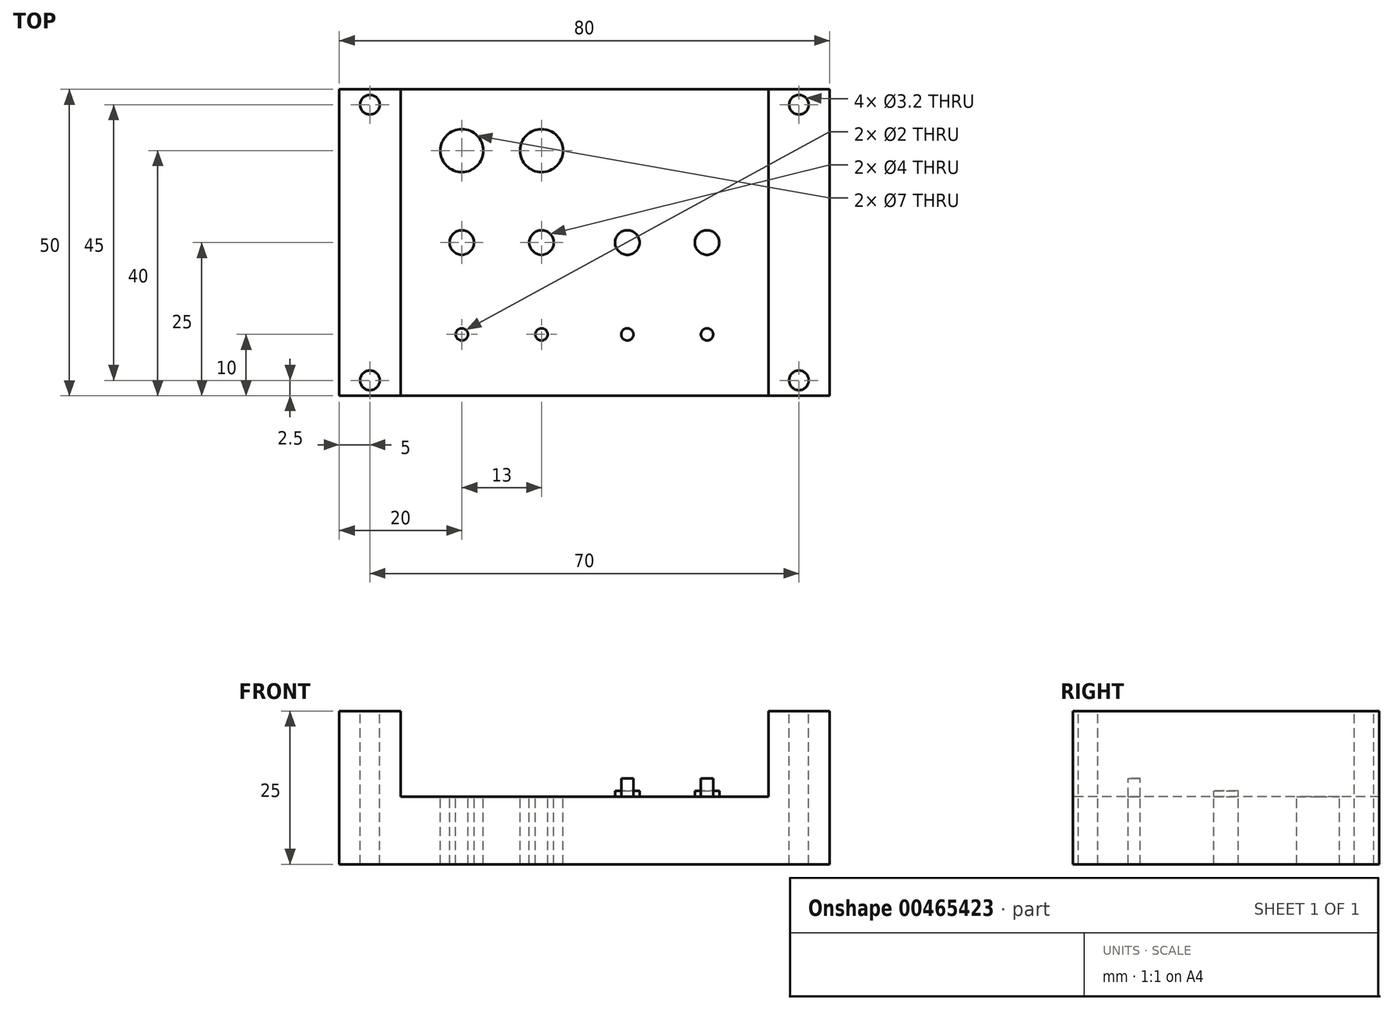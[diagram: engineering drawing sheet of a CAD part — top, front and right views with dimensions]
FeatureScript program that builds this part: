
annotation { "Feature Type Name" : "Feature", "Feature Type Description" : "" }
export const myFeature = defineFeature(function(context is Context, id is Id, definition is map)
    precondition{}
    {
        {
            var Q0;
            Q0=qCreatedBy(makeId("Top.planeOp"),FACE);
            var sketch = newSketch(context, id + "F0", { "sketchPlane" : qUnion([Q0])});
            skLineSegment(sketch, "E0.bottom", {"start": v(40, -25) * mm, "end": v(-40, -25) * mm});
            skLineSegment(sketch, "E0.top", {"start": v(40, 25) * mm, "end": v(-40, 25) * mm});
            skLineSegment(sketch, "E0.left", {"start": v(40, -25) * mm, "end": v(40, 25) * mm});
            skLineSegment(sketch, "E0.right", {"start": v(-40, -25) * mm, "end": v(-40, 25) * mm});
            skPoint(sketch, "E0.middle", {"position": v(0, 0) * mm});
            skLineSegment(sketch, "E1.bottom", {"start": v(30, 25) * mm, "end": v(40, 25) * mm});
            skLineSegment(sketch, "E1.top", {"start": v(30, -25) * mm, "end": v(40, -25) * mm});
            skLineSegment(sketch, "E1.left", {"start": v(30, 25) * mm, "end": v(30, -25) * mm});
            skLineSegment(sketch, "E1.right", {"start": v(40, 25) * mm, "end": v(40, -25) * mm});
            skCircle(sketch, "E2", {"center": v(7, -15) * mm, "radius": 1 * mm});
            skCircle(sketch, "E3", {"center": v(20, -15) * mm, "radius": 1 * mm});
            skCircle(sketch, "E4", {"center": v(7, 0) * mm, "radius": 2 * mm});
            skCircle(sketch, "E5", {"center": v(20, 0) * mm, "radius": 2 * mm});
            skCircle(sketch, "E6", {"center": v(7, 15) * mm, "radius": 3.5 * mm});
            skCircle(sketch, "E7", {"center": v(20, 15) * mm, "radius": 3.5 * mm});
            skLineSegment(sketch, "E8", {"start": v(7, -25) * mm, "end": v(7, 25) * mm, "construction": true});
            skLineSegment(sketch, "E9", {"start": v(20, -25) * mm, "end": v(20, 25) * mm, "construction": true});
            skCircle(sketch, "E10", {"center": v(35, -22.5) * mm, "radius": 1.6 * mm});
            skLineSegment(sketch, "E11", {"start": v(0, -15) * mm, "end": v(30, -15) * mm, "construction": true});
            skLineSegment(sketch, "E12.MirrorCS", {"start": v(0, 15) * mm, "end": v(30, 15) * mm, "construction": true});
            skLineSegment(sketch, "E13", {"start": v(30, -22.5) * mm, "end": v(40, -22.5) * mm, "construction": true});
            skCircle(sketch, "E14.MirrorC", {"center": v(35, 22.5) * mm, "radius": 1.6 * mm});
            skCircle(sketch, "E15.MirrorC", {"center": v(-7, 15) * mm, "radius": 3.5 * mm});
            skCircle(sketch, "E16.MirrorC", {"center": v(-20, 15) * mm, "radius": 3.5 * mm});
            skCircle(sketch, "E17.MirrorC", {"center": v(-7, 0) * mm, "radius": 2 * mm});
            skCircle(sketch, "E18.MirrorC", {"center": v(-20, 0) * mm, "radius": 2 * mm});
            skCircle(sketch, "E19.MirrorC", {"center": v(-7, -15) * mm, "radius": 1 * mm});
            skCircle(sketch, "E20.MirrorC", {"center": v(-20, -15) * mm, "radius": 1 * mm});
            skLineSegment(sketch, "E21.MirrorCS", {"start": v(-30, 25) * mm, "end": v(-30, -25) * mm});
            skCircle(sketch, "E22.MirrorC", {"center": v(-35, 22.5) * mm, "radius": 1.6 * mm});
            skCircle(sketch, "E23.MirrorC", {"center": v(-35, -22.5) * mm, "radius": 1.6 * mm});
            skSolve(sketch);
        }
        {
            var Q0;
            {var subQ0=sQuery(id+"F0.wireOp",EDGE,"E1.left");var subQ1=makeQuery(id+"F0.imprint","IMPRINT",EDGE,{"derivedFrom":subQ0});var subQ4=sQuery(id+"F0.wireOp",EDGE,"E0.left");var subQ9=sQuery(id+"F0.wireOp",EDGE,"E0.right");Q0=qUnion([makeQuery(id+"F0.imprint","IMPRINT",FACE,{"disambiguationData":[TD([[subQ1,-1.0]])]}),makeQuery(id+"F0.imprint","IMPRINT",FACE,{"disambiguationData":[TD([[makeQuery(id+"F0.imprint","IMPRINT",EDGE,{"derivedFrom":subQ9}),-1.0]])]}),makeQuery(id+"F0.imprint","IMPRINT",FACE,{"disambiguationData":[TD([[makeQuery(id+"F0.imprint","IMPRINT",EDGE,{"derivedFrom":subQ4}),1.0]])]})]);}
            var Q1;
            Q1=makeQuery(id+"F0.imprint","IMPRINT",FACE,{"disambiguationData":[TD([[makeQuery(id+"F0.imprint","IMPRINT",EDGE,{"derivedFrom":sQuery(id+"F0.wireOp",EDGE,"E16.MirrorC")}),-1.0]])]});
            var Q2;
            Q2=makeQuery(id+"F0.imprint","IMPRINT",FACE,{"disambiguationData":[TD([[makeQuery(id+"F0.imprint","IMPRINT",EDGE,{"derivedFrom":sQuery(id+"F0.wireOp",EDGE,"E15.MirrorC")}),-1.0]])]});
            var Q3;
            Q3=makeQuery(id+"F0.imprint","IMPRINT",FACE,{"disambiguationData":[TD([[makeQuery(id+"F0.imprint","IMPRINT",EDGE,{"derivedFrom":sQuery(id+"F0.wireOp",EDGE,"E6")}),1.0]])]});
            var Q4;
            Q4=makeQuery(id+"F0.imprint","IMPRINT",FACE,{"disambiguationData":[TD([[makeQuery(id+"F0.imprint","IMPRINT",EDGE,{"derivedFrom":sQuery(id+"F0.wireOp",EDGE,"E7")}),1.0]])]});
            var Q5;
            Q5=makeQuery(id+"F0.imprint","IMPRINT",FACE,{"disambiguationData":[TD([[makeQuery(id+"F0.imprint","IMPRINT",EDGE,{"derivedFrom":sQuery(id+"F0.wireOp",EDGE,"E4")}),1.0]])]});
            var Q6;
            Q6=makeQuery(id+"F0.imprint","IMPRINT",FACE,{"disambiguationData":[TD([[makeQuery(id+"F0.imprint","IMPRINT",EDGE,{"derivedFrom":sQuery(id+"F0.wireOp",EDGE,"E5")}),1.0]])]});
            var Q7;
            Q7=makeQuery(id+"F0.imprint","IMPRINT",FACE,{"disambiguationData":[TD([[makeQuery(id+"F0.imprint","IMPRINT",EDGE,{"derivedFrom":sQuery(id+"F0.wireOp",EDGE,"E17.MirrorC")}),-1.0]])]});
            var Q8;
            Q8=makeQuery(id+"F0.imprint","IMPRINT",FACE,{"disambiguationData":[TD([[makeQuery(id+"F0.imprint","IMPRINT",EDGE,{"derivedFrom":sQuery(id+"F0.wireOp",EDGE,"E18.MirrorC")}),-1.0]])]});
            var Q9;
            Q9=makeQuery(id+"F0.imprint","IMPRINT",FACE,{"disambiguationData":[TD([[makeQuery(id+"F0.imprint","IMPRINT",EDGE,{"derivedFrom":sQuery(id+"F0.wireOp",EDGE,"E20.MirrorC")}),-1.0]])]});
            var Q10;
            Q10=makeQuery(id+"F0.imprint","IMPRINT",FACE,{"disambiguationData":[TD([[makeQuery(id+"F0.imprint","IMPRINT",EDGE,{"derivedFrom":sQuery(id+"F0.wireOp",EDGE,"E19.MirrorC")}),-1.0]])]});
            var Q11;
            Q11=makeQuery(id+"F0.imprint","IMPRINT",FACE,{"disambiguationData":[TD([[makeQuery(id+"F0.imprint","IMPRINT",EDGE,{"derivedFrom":sQuery(id+"F0.wireOp",EDGE,"E2")}),1.0]])]});
            var Q12;
            Q12=makeQuery(id+"F0.imprint","IMPRINT",FACE,{"disambiguationData":[TD([[makeQuery(id+"F0.imprint","IMPRINT",EDGE,{"derivedFrom":sQuery(id+"F0.wireOp",EDGE,"E3")}),1.0]])]});
            extrude(context, id + "F1", {"entities" : qUnion([Q0, Q1, Q2, Q3, Q4, Q5, Q6, Q7, Q8, Q9, Q10, Q11, Q12]), "oppositeDirection" : true, "depth" : 15 * mm, "offsetDistance" : 25 * mm});
        }
        {
            var Q0;
            {var subQ1=sQuery(id+"F0.wireOp",EDGE,"E0.right");Q0=makeQuery(id+"F0.imprint","IMPRINT",FACE,{"disambiguationData":[TD([[makeQuery(id+"F0.imprint","IMPRINT",EDGE,{"derivedFrom":subQ1}),-1.0]])]});}
            var Q1;
            {var subQ2=sQuery(id+"F0.wireOp",EDGE,"E0.left");Q1=makeQuery(id+"F0.imprint","IMPRINT",FACE,{"disambiguationData":[TD([[makeQuery(id+"F0.imprint","IMPRINT",EDGE,{"derivedFrom":subQ2}),1.0]])]});}
            extrude(context, id + "F2", {"entities" : qUnion([Q0, Q1]), "operationType" : NewBodyOperationType.ADD, "depth" : 10 * mm, "offsetDistance" : 25 * mm});
        }
        {
            var Q0;
            Q0=makeQuery(id+"F0.imprint","IMPRINT",FACE,{"disambiguationData":[TD([[makeQuery(id+"F0.imprint","IMPRINT",EDGE,{"derivedFrom":sQuery(id+"F0.wireOp",EDGE,"E16.MirrorC")}),-1.0]])]});
            var Q1;
            Q1=makeQuery(id+"F0.imprint","IMPRINT",FACE,{"disambiguationData":[TD([[makeQuery(id+"F0.imprint","IMPRINT",EDGE,{"derivedFrom":sQuery(id+"F0.wireOp",EDGE,"E15.MirrorC")}),-1.0]])]});
            var Q2;
            Q2=makeQuery(id+"F0.imprint","IMPRINT",FACE,{"disambiguationData":[TD([[makeQuery(id+"F0.imprint","IMPRINT",EDGE,{"derivedFrom":sQuery(id+"F0.wireOp",EDGE,"E6")}),1.0]])]});
            var Q3;
            Q3=makeQuery(id+"F0.imprint","IMPRINT",FACE,{"disambiguationData":[TD([[makeQuery(id+"F0.imprint","IMPRINT",EDGE,{"derivedFrom":sQuery(id+"F0.wireOp",EDGE,"E7")}),1.0]])]});
            extrude(context, id + "F3", {"entities" : qUnion([Q0, Q1, Q2, Q3]), "operationType" : NewBodyOperationType.REMOVE, "oppositeDirection" : true, "depth" : 4 * mm, "offsetDistance" : 25 * mm});
        }
        {
            var Q0;
            Q0=makeQuery(id+"F0.imprint","IMPRINT",FACE,{"disambiguationData":[TD([[makeQuery(id+"F0.imprint","IMPRINT",EDGE,{"derivedFrom":sQuery(id+"F0.wireOp",EDGE,"E18.MirrorC")}),-1.0]])]});
            var Q1;
            Q1=makeQuery(id+"F0.imprint","IMPRINT",FACE,{"disambiguationData":[TD([[makeQuery(id+"F0.imprint","IMPRINT",EDGE,{"derivedFrom":sQuery(id+"F0.wireOp",EDGE,"E17.MirrorC")}),-1.0]])]});
            var Q2;
            Q2=makeQuery(id+"F0.imprint","IMPRINT",FACE,{"disambiguationData":[TD([[makeQuery(id+"F0.imprint","IMPRINT",EDGE,{"derivedFrom":sQuery(id+"F0.wireOp",EDGE,"E4")}),1.0]])]});
            var Q3;
            Q3=makeQuery(id+"F0.imprint","IMPRINT",FACE,{"disambiguationData":[TD([[makeQuery(id+"F0.imprint","IMPRINT",EDGE,{"derivedFrom":sQuery(id+"F0.wireOp",EDGE,"E5")}),1.0]])]});
            extrude(context, id + "F4", {"entities" : qUnion([Q0, Q1, Q2, Q3]), "operationType" : NewBodyOperationType.REMOVE, "oppositeDirection" : true, "depth" : 3 * mm, "offsetDistance" : 25 * mm});
        }
        {
            var Q0;
            Q0=makeQuery(id+"F0.imprint","IMPRINT",FACE,{"disambiguationData":[TD([[makeQuery(id+"F0.imprint","IMPRINT",EDGE,{"derivedFrom":sQuery(id+"F0.wireOp",EDGE,"E20.MirrorC")}),-1.0]])]});
            var Q1;
            Q1=makeQuery(id+"F0.imprint","IMPRINT",FACE,{"disambiguationData":[TD([[makeQuery(id+"F0.imprint","IMPRINT",EDGE,{"derivedFrom":sQuery(id+"F0.wireOp",EDGE,"E19.MirrorC")}),-1.0]])]});
            var Q2;
            Q2=makeQuery(id+"F0.imprint","IMPRINT",FACE,{"disambiguationData":[TD([[makeQuery(id+"F0.imprint","IMPRINT",EDGE,{"derivedFrom":sQuery(id+"F0.wireOp",EDGE,"E2")}),1.0]])]});
            var Q3;
            Q3=makeQuery(id+"F0.imprint","IMPRINT",FACE,{"disambiguationData":[TD([[makeQuery(id+"F0.imprint","IMPRINT",EDGE,{"derivedFrom":sQuery(id+"F0.wireOp",EDGE,"E3")}),1.0]])]});
            extrude(context, id + "F5", {"entities" : qUnion([Q0, Q1, Q2, Q3]), "operationType" : NewBodyOperationType.REMOVE, "oppositeDirection" : true, "depth" : 1 * mm, "offsetDistance" : 25 * mm});
        }
    });
